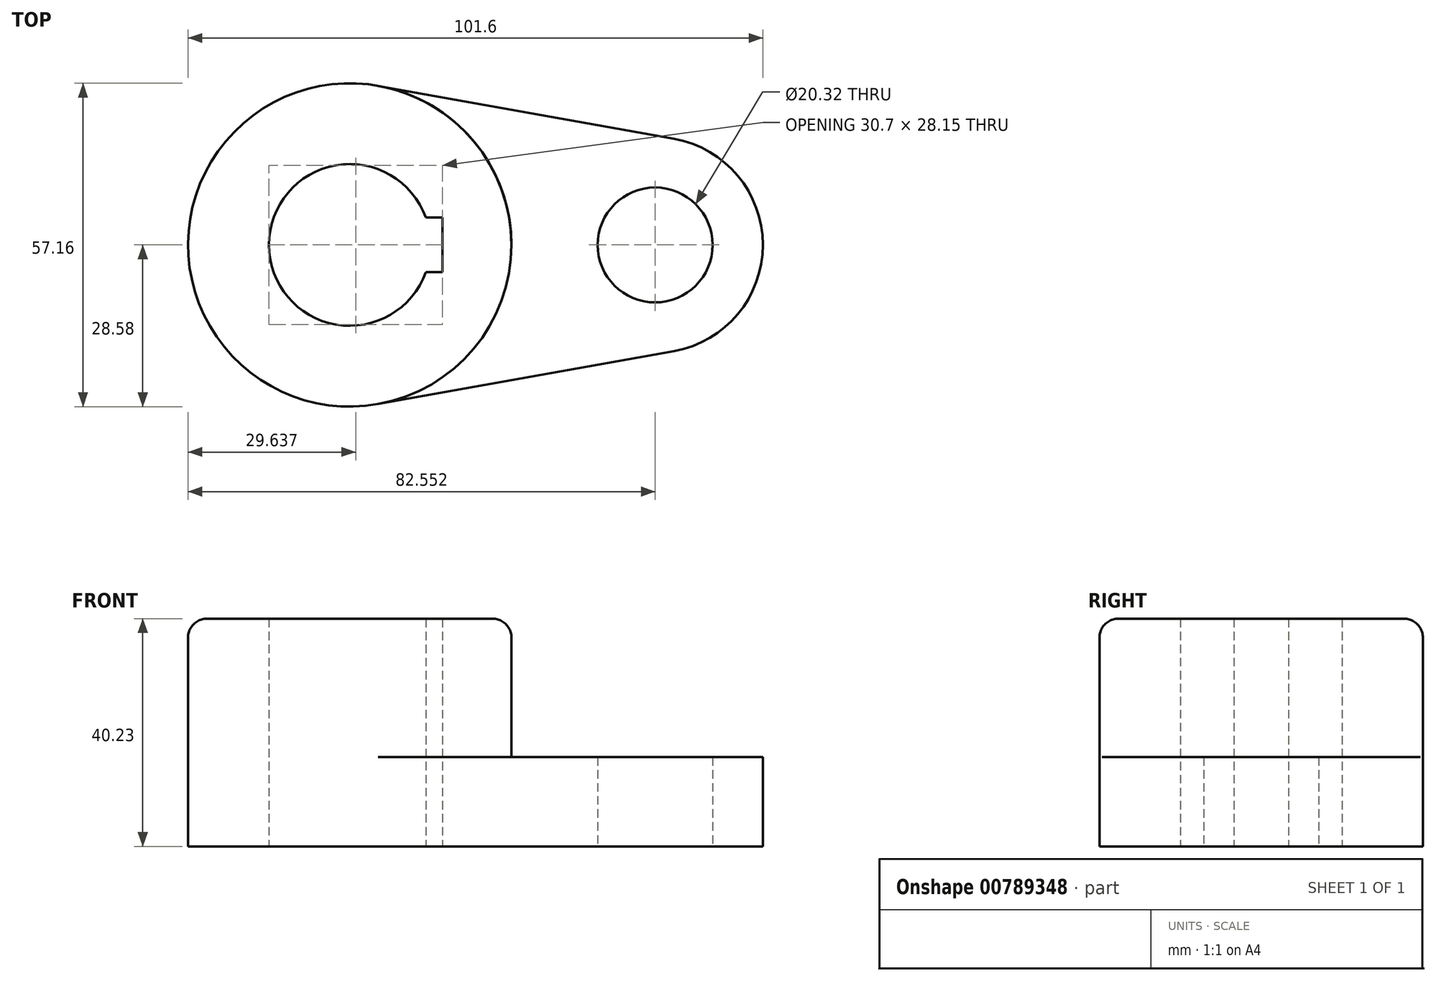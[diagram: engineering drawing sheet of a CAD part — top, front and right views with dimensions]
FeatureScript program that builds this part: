
annotation { "Feature Type Name" : "Feature", "Feature Type Description" : "" }
export const myFeature = defineFeature(function(context is Context, id is Id, definition is map)
    precondition{}
    {
        {
            var Q0;
            Q0=qCreatedBy(makeId("Top.planeOp"),FACE);
            var sketch = newSketch(context, id + "F0", { "sketchPlane" : qUnion([Q0])});
            skCircle(sketch, "E0", {"center": v(3.42, 0) * mm, "radius": 19.05 * mm});
            skCircle(sketch, "E1", {"center": v(3.42, 0) * mm, "radius": 10.16 * mm});
            skCircle(sketch, "E2", {"center": v(-50.55, 0) * mm, "radius": 28.58 * mm});
            skArc(sketch, "E3", {"start": v(-37.1, 4.83) * mm, "mid": v(-64.84, 0) * mm, "end": v(-37.1, -4.83) * mm});
            skLineSegment(sketch, "E4", {"start": v(-45.51, 28.13) * mm, "end": v(10.17, 18.14) * mm});
            skLineSegment(sketch, "E5", {"start": v(-45.51, -28.13) * mm, "end": v(6.78, -18.75) * mm});
            skLineSegment(sketch, "E6.bottom", {"start": v(-34.14, 4.83) * mm, "end": v(-64, 4.83) * mm});
            skLineSegment(sketch, "E6.top", {"start": v(-34.14, -4.83) * mm, "end": v(-64, -4.83) * mm});
            skLineSegment(sketch, "E6.left", {"start": v(-34.14, 4.83) * mm, "end": v(-34.14, -4.83) * mm});
            skPoint(sketch, "E7.orphan", {"position": v(-66.96, -4.83) * mm});
            skPoint(sketch, "E8.orphan", {"position": v(-66.96, 4.83) * mm});
            skSolve(sketch);
        }
        {
            var Q0;
            {var subQ9=sQuery(id+"F0.wireOp",EDGE,"E6.left");Q0=makeQuery(id+"F0.imprint","IMPRINT",FACE,{"disambiguationData":[TD([[makeQuery(id+"F0.imprint","IMPRINT",EDGE,{"derivedFrom":subQ9}),1.0]])]});}
            extrude(context, id + "F1", {"entities" : qUnion([Q0]), "depth" : 40.23 * mm, "offsetDistance" : 25.4 * mm});
        }
        {
            var Q0;
            {var subQ0=sQuery(id+"F0.wireOp",EDGE,"E5");Q0=makeQuery(id+"F0.imprint","IMPRINT",FACE,{"disambiguationData":[TD([[makeQuery(id+"F0.imprint","IMPRINT",EDGE,{"derivedFrom":subQ0}),1.0]])]});}
            var Q1;
            Q1=makeQuery(id+"F0.imprint","IMPRINT",FACE,{"disambiguationData":[TD([[makeQuery(id+"F0.imprint","IMPRINT",EDGE,{"derivedFrom":sQuery(id+"F0.wireOp",EDGE,"E1")}),-1.0]])]});
            extrude(context, id + "F2", {"entities" : qUnion([Q0, Q1]), "operationType" : NewBodyOperationType.ADD, "depth" : 15.77 * mm, "offsetDistance" : 25.4 * mm});
        }
        {
            var Q0;
            Q0=makeQuery(id+"F1.opExtrude","CAP_EDGE",EDGE,{"disambiguationData":[OSD([sQuery(id+"F0.wireOp",EDGE,"E2")])],"isStart":false});
            fillet(context, id + "F3", {"entities" : qUnion([Q0]), "radius" : 3.3 * mm, "tangentPropagation" : true, "allowEdgeOverflow" : false});
        }
    });
